# Revit family: Sanitary_Shower-screens_Duscholux_DuschoGredel_DuschoEryx _Separator-slider-door-bath
name_source: partatom
category: Plumbing Fixtures
revit_build: Autodesk Revit 2017 (Build: 20160225_1515(x64)
units: mm (PartAtom-declared; Revit-internal decimal feet)

## family parameters
Always vertical = Yes
Cut with Voids When Loaded = No
OmniClass Number = 23.45.00.00
OmniClass Title = Sanitary, Laundry, and Cleaning Equipment
Part Type = Normal
Room Calculation Point = No
Round Connector Dimension = Use Diameter
Shared = No
Work Plane-Based = No

## types (4) — shared parameters
Assembly Code = C1030200
Brand = Duscholux
Certified Quality UNE EN 14428 = http://www.duscholux.es
Components = European components
Configuration enclosure = http://configuratumampara.duscholux.es
Description = 1 fixed + slider door for a recess (Bath)
Design country = Spain / Germany
Edition number = 1
Environmental Management ISO 14001 = ECOEMBES Certificate
Fact Sheet = http://blob.duscholux.es
Glass Material = Glass Material Duscholux
Glass in Building UNE EN 12150 = CE Conformity marking
IFC Classification = Furnishing Element
Image = http://www.duscholux.es
Logo visibility = Yes
Maintenance and Cleaning = http://www.duscholux.es
Manufacturer = Duscholux Ibérica, S.A.
Manufacturer country = Spain
Manufacturer name = Duscholux Ibérica, S.A.
Max Height = 1600 mm  [stored 5.24934 ft]
Model = DuschoEryx
NBS Reference Code = 45-35-70
NBS Reference Description = Shower Enclosures
Net Weight (Kg) = 40.7
Opening System = Sliding
Opening System Image = http://blob.duscholux.es
Optional = Towel rail / Shelf
Product family = Duscho Gredel
Product group = Slider door (Separator for Bath)
Products = http://www.duscholux.es
Ref. = 6OI / 6OD
Serie = Duscho Gredel
Technical Inspection Certificate (Applus) = http://www.duscholux.es
Text logo visibility = Yes
Thickness Safety Glass Fixed Panel = 8 mm  [stored 0.0262467 ft]
Thickness Safety Glass Sliding = 5 mm  [stored 0.0164042 ft]
UNSPSC Code = 30181507
URL = http://www.duscholux.es
Uniclass 2015 Code = PR-40-20-06-79
Uniclass 2015 Description = Shower Enclosures
zero-valued in all types: Opening Door, Opening Percentage

## per-type parameters (varying)
| type | Accesories Material | Bath Height | D1 | Frame Material | Handle Height | Handle Material | Height | Min Max Width | Sliding Door Width | Vertical Support Lenght | Visibility Vertical support | Wall Support lenght | Width |
| Silver Matt Aluminium Finish | Chrome Finish | 450 mm  [stored 1.47638 ft] | 250 mm  [stored 0.82021 ft] | Silver Matt Finish | 1250 mm  [stored 4.10105 ft] | Chrome Finish | 1800 mm  [stored 5.90551 ft] | 1000 mm  [stored 3.28084 ft] | 472 mm | 600 mm | No | 354 mm | 1000 mm  [stored 3.28084 ft] |
| Platinum Aluminium Finish | Silver Matt Finish | 400 mm  [stored 1.31234 ft] | 250 mm  [stored 0.82021 ft] | Platinium Aluminium Finish | 1200 mm | Chrome Finish | 1800 mm  [stored 5.90551 ft] | 800 mm  [stored 2.62467 ft] | 372 mm  [stored 1.22047 ft] | 600 mm | No | 354 mm | 800 mm  [stored 2.62467 ft] |
| White Aluminium Finish | White Finish | 400 mm  [stored 1.31234 ft] | 212 mm | White Finish | 1200 mm | White Finish | 1600 mm  [stored 5.24934 ft] | 1300 mm  [stored 4.26509 ft] | 622 mm  [stored 2.04068 ft] | 400 mm  [stored 1.31234 ft] | Yes | 300 mm | 1300 mm  [stored 4.26509 ft] |
| Black Aluminium Finish | Chrome Finish | 400 mm  [stored 1.31234 ft] | 250 mm  [stored 0.82021 ft] | Black Aluminium Finish | 1200 mm | Chrome Finish | 1800 mm  [stored 5.90551 ft] | 1000 mm  [stored 3.28084 ft] | 472 mm | 600 mm | No | 354 mm | 1000 mm  [stored 3.28084 ft] |

note: [stored X ft] marks values corroborated as IEEE doubles in the binary element streams (Revit-internal decimal feet)

## geometry (parser evidence)
native form markers: Sweep x3
no freeform markers — native parametric forms only
